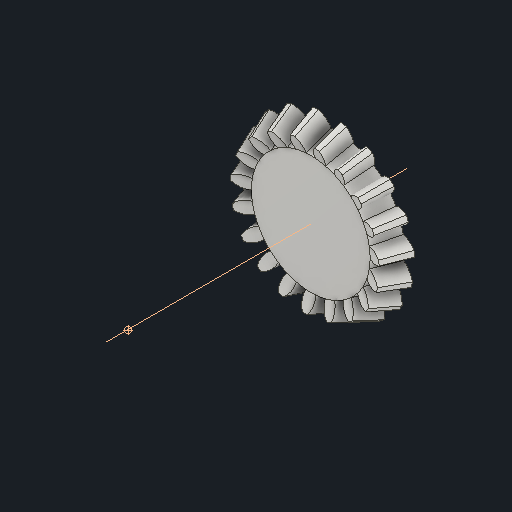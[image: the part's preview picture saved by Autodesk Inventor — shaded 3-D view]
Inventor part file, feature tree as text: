
AUTODESK INVENTOR PART (.ipt)
format: ipt  version: 2022 (Build 260153000, 153)  size: 559,104 bytes
history: native  units: mm
features: other x24, loft x2, pattern_circular x2, sketch x1
ambient origin geometry x6: Origin, XZ Plane, X Axis, Y Axis, Z Axis, Center Point
bodies: Solid1 (feature_tree)
feature tree (29):
  other  "Top Point"
  other  "Mesh Plane2"
  other  "Teeth Body"
  other  "Start Point"
  other  "Tooth Plane"
  other  "Start Sketch"
  other  "End Point"
  other  "3D Sketch Right"
  other  "End Plane Right"
  loft  "Loft Right"
  pattern_circular  "Circular Pattern Right"  [2 undecoded]
  other  "3D Sketch Left"
  other  "End Plane Left"
  loft  "Loft Left"
  pattern_circular  "Circular Pattern Left"  [2 undecoded]
  other  "Fix Body"
  other  "Mesh Plane"
  other  "Top Plane"
  other  "Teeth Body Sketch"
  other  "End Plane"
  other  "End Sketch"
  other  "Helical Curve Left"
  other  "End Sketch Left"
  other  "Body Sketch"
  sketch  "Sketch6"  dims[d0=47.5mm d1=40.16154mm d2=50.389413mm d3=8.0mm d4=59.428137mm d5=90.0deg d7=6.612538mm d8=8.167518mm d9=22.385367mm d11=8.275mm d12=5.764574mm d15=7.120149mm d16=19.514761mm d17=0.0mm d18=90.0deg d19=0.0mm d20=90.0deg d21=190.0mm d22=360.0deg d26=357.584802mm d27=7.69415mm d28=47.5mm d29=-3.769093mm d30=5.764574mm d31=7.120149mm d32=19.514761mm d35=0.0mm d37=0.0mm d39=0.0mm d40=90.0deg d41=190.0mm d42=360.0deg d46=90.0deg d47=90.0deg d48=0.0mm d49=0.0mm d50=90.0deg d51=1.65347mm d52=0.0mm d53=0.0mm d54=0.0mm d56=20.521955mm d57=28.746717mm d58=20.936717mm d59=25.060358mm d60=18.25188mm d61=25.060358mm d62=18.25188mm d65=357.584802mm d66=31.5mm d67=47.5mm d68=-3.769093mm d69=7.69415mm d70=7.120149mm d71=19.514761mm d72=5.764574mm d73=18.25188mm d74=25.060358mm d75=0.0mm d77=0.0mm d79=0.0mm d80=90.0deg d81=190.0mm d82=360.0deg d84=10.0mm d85=20.0mm d86=20.0mm d87=10.0mm d88=0.0mm d89=0.0mm d90=90.0deg d91=90.0deg d92=90.0deg d93=90.0deg]
  other  "Srf1"
  other  "Helical Curve Right"
  other  "End Sketch Right"
  other  "Pitch Diameter"
note: 4 required parameter values undecoded (feature->parameter linkage not recoverable at this tier; creation-order binding heuristic only, values carry confidence <= 0.55)
